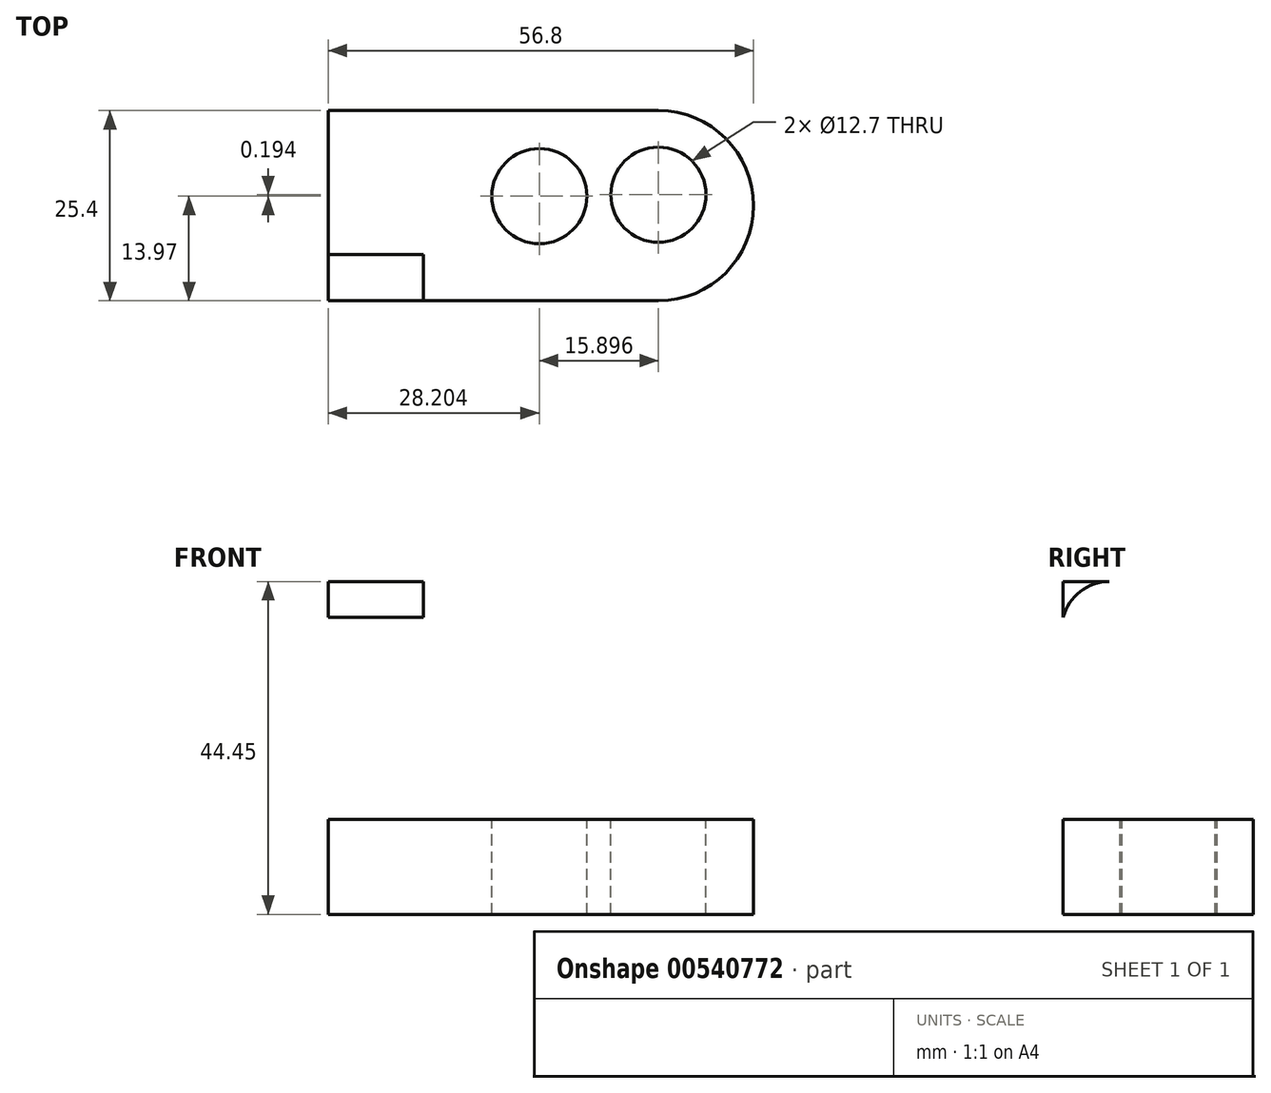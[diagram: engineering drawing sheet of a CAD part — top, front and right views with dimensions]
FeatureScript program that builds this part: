
annotation { "Feature Type Name" : "Feature", "Feature Type Description" : "" }
export const myFeature = defineFeature(function(context is Context, id is Id, definition is map)
    precondition{}
    {
        {
            var Q0;
            Q0=qCreatedBy(makeId("Front.planeOp"),FACE);
            var sketch = newSketch(context, id + "F0", { "sketchPlane" : qUnion([Q0])});
            skLineSegment(sketch, "E0", {"start": v(0, 0) * mm, "end": v(0, 44.45) * mm});
            skLineSegment(sketch, "E1", {"start": v(0, 44.45) * mm, "end": v(12.7, 44.45) * mm});
            skLineSegment(sketch, "E2", {"start": v(12.7, 44.45) * mm, "end": v(12.7, 12.7) * mm});
            skLineSegment(sketch, "E3", {"start": v(12.7, 12.7) * mm, "end": v(57.15, 12.7) * mm});
            skLineSegment(sketch, "E4", {"start": v(57.15, 12.7) * mm, "end": v(57.15, 0) * mm});
            skLineSegment(sketch, "E5", {"start": v(57.15, 0) * mm, "end": v(0, 0) * mm});
            skSolve(sketch);
        }
        {
            var Q0;
            Q0=makeQuery(id+"F0.imprint","IMPRINT",FACE,{"disambiguationData":[TD([[makeQuery(id+"F0.imprint","IMPRINT",EDGE,{"derivedFrom":sQuery(id+"F0.wireOp",EDGE,"E0")}),-1.0]])]});
            extrude(context, id + "F1", {"entities" : qUnion([Q0]), "depth" : 25.4 * mm, "offsetDistance" : 25.4 * mm});
        }
        {
            var Q0;
            Q0=makeQuery(id+"F1.opExtrude","SWEPT_FACE",FACE,{"disambiguationData":[OSD([sQuery(id+"F0.wireOp",EDGE,"E2")])]});
            var sketch = newSketch(context, id + "F2", { "sketchPlane" : qUnion([Q0])});
            skCircle(sketch, "E6", {"center": v(-12.9, 28.57) * mm, "radius": 6.35 * mm});
            skPoint(sketch, "E6.centerSnap0", {"position": v(-25.4, 28.57) * mm});
            skLineSegment(sketch, "E7", {"start": v(-19.25, 28.57) * mm, "end": v(-19.25, 44.45) * mm});
            skLineSegment(sketch, "E8", {"start": v(-6.55, 28.57) * mm, "end": v(-6.55, 44.45) * mm});
            skLineSegment(sketch, "E9", {"start": v(-6.55, 44.45) * mm, "end": v(-19.25, 44.45) * mm});
            skArc(sketch, "E10", {"start": v(-19.25, 44.45) * mm, "mid": v(-24.27, 41.99) * mm, "end": v(-25.4, 36.51) * mm});
            skPoint(sketch, "E10.endSnap0", {"position": v(-19.25, 36.51) * mm});
            skArc(sketch, "E11", {"start": v(0, 38.1) * mm, "mid": v(-1.99, 42.6) * mm, "end": v(-6.55, 44.45) * mm});
            skSolve(sketch);
        }
        {
            var Q0;
            {var subQ0=sQuery(id+"F2.wireOp",EDGE,"E6");var subQ1=makeQuery(id+"F2.imprint","INTERSECT",VERTEX,{"derivedFrom":[subQ0,sQuery(id+"F2.wireOp",EDGE,"E7")]});Q0=makeQuery(id+"F2.imprint","IMPRINT",FACE,{"disambiguationData":[TD([[makeQuery(id+"F2.imprint","IMPRINT",EDGE,{"disambiguationData":[TD([[subQ1,1.0]])],"derivedFrom":subQ0}),1.0]])]});}
            var Q1;
            {var subQ0=sQuery(id+"F2.wireOp",EDGE,"E7");Q1=makeQuery(id+"F2.imprint","IMPRINT",FACE,{"disambiguationData":[TD([[makeQuery(id+"F2.imprint","IMPRINT",EDGE,{"derivedFrom":subQ0}),-1.0]])]});}
            var Q2;
            {var subQ0=sQuery(id+"F2.wireOp",EDGE,"E11");Q2=makeQuery(id+"F2.imprint","IMPRINT",FACE,{"disambiguationData":[TD([[makeQuery(id+"F2.imprint","IMPRINT",EDGE,{"derivedFrom":subQ0}),-1.0]])]});}
            var Q3;
            {var subQ0=sQuery(id+"F2.wireOp",EDGE,"E10");var subQ1=sQuery(id+"F0.wireOp",EDGE,"E2");var subQ4=makeQuery(id+"F1.opExtrude","CAP_EDGE",EDGE,{"disambiguationData":[OSD([subQ1])],"isStart":false});var subQ5=makeQuery(id+"F2.imprint","INTERSECT",VERTEX,{"disambiguationData":[OD(1.0)],"derivedFrom":[subQ4,subQ0]});Q3=makeQuery(id+"F2.imprint","IMPRINT",FACE,{"disambiguationData":[TD([[makeQuery(id+"F2.imprint","IMPRINT",EDGE,{"disambiguationData":[TD([[subQ5,1.0]])],"derivedFrom":subQ4}),1.0]])]});}
            extrude(context, id + "F3", {"entities" : qUnion([Q0, Q1, Q2, Q3]), "operationType" : NewBodyOperationType.REMOVE, "oppositeDirection" : true, "depth" : 12.7 * mm, "offsetDistance" : 25.4 * mm});
        }
        {
            var Q0;
            Q0=makeQuery(id+"F1.opExtrude","SWEPT_FACE",FACE,{"disambiguationData":[OSD([sQuery(id+"F0.wireOp",EDGE,"E3")])]});
            var sketch = newSketch(context, id + "F4", { "sketchPlane" : qUnion([Q0])});
            skCircle(sketch, "E12", {"center": v(28.2, -11.43) * mm, "radius": 6.35 * mm});
            skCircle(sketch, "E13", {"center": v(44.1, -11.24) * mm, "radius": 6.35 * mm});
            skArc(sketch, "E14", {"start": v(44.1, -25.4) * mm, "mid": v(56.8, -12.7) * mm, "end": v(44.1, 0) * mm});
            skSolve(sketch);
        }
        {
            var Q0;
            Q0=makeQuery(id+"F4.imprint","IMPRINT",FACE,{"disambiguationData":[TD([[makeQuery(id+"F4.imprint","IMPRINT",EDGE,{"derivedFrom":sQuery(id+"F4.wireOp",EDGE,"E12")}),1.0]])]});
            var Q1;
            Q1=makeQuery(id+"F4.imprint","IMPRINT",FACE,{"disambiguationData":[TD([[makeQuery(id+"F4.imprint","IMPRINT",EDGE,{"derivedFrom":sQuery(id+"F4.wireOp",EDGE,"E13")}),1.0]])]});
            var Q2;
            {var subQ0=sQuery(id+"F4.wireOp",EDGE,"E14");Q2=makeQuery(id+"F4.imprint","IMPRINT",FACE,{"disambiguationData":[TD([[makeQuery(id+"F4.imprint","IMPRINT",EDGE,{"derivedFrom":subQ0}),-1.0]])]});}
            extrude(context, id + "F5", {"entities" : qUnion([Q0, Q1, Q2]), "operationType" : NewBodyOperationType.REMOVE, "oppositeDirection" : true, "depth" : 12.7 * mm, "offsetDistance" : 25.4 * mm});
        }
    });
